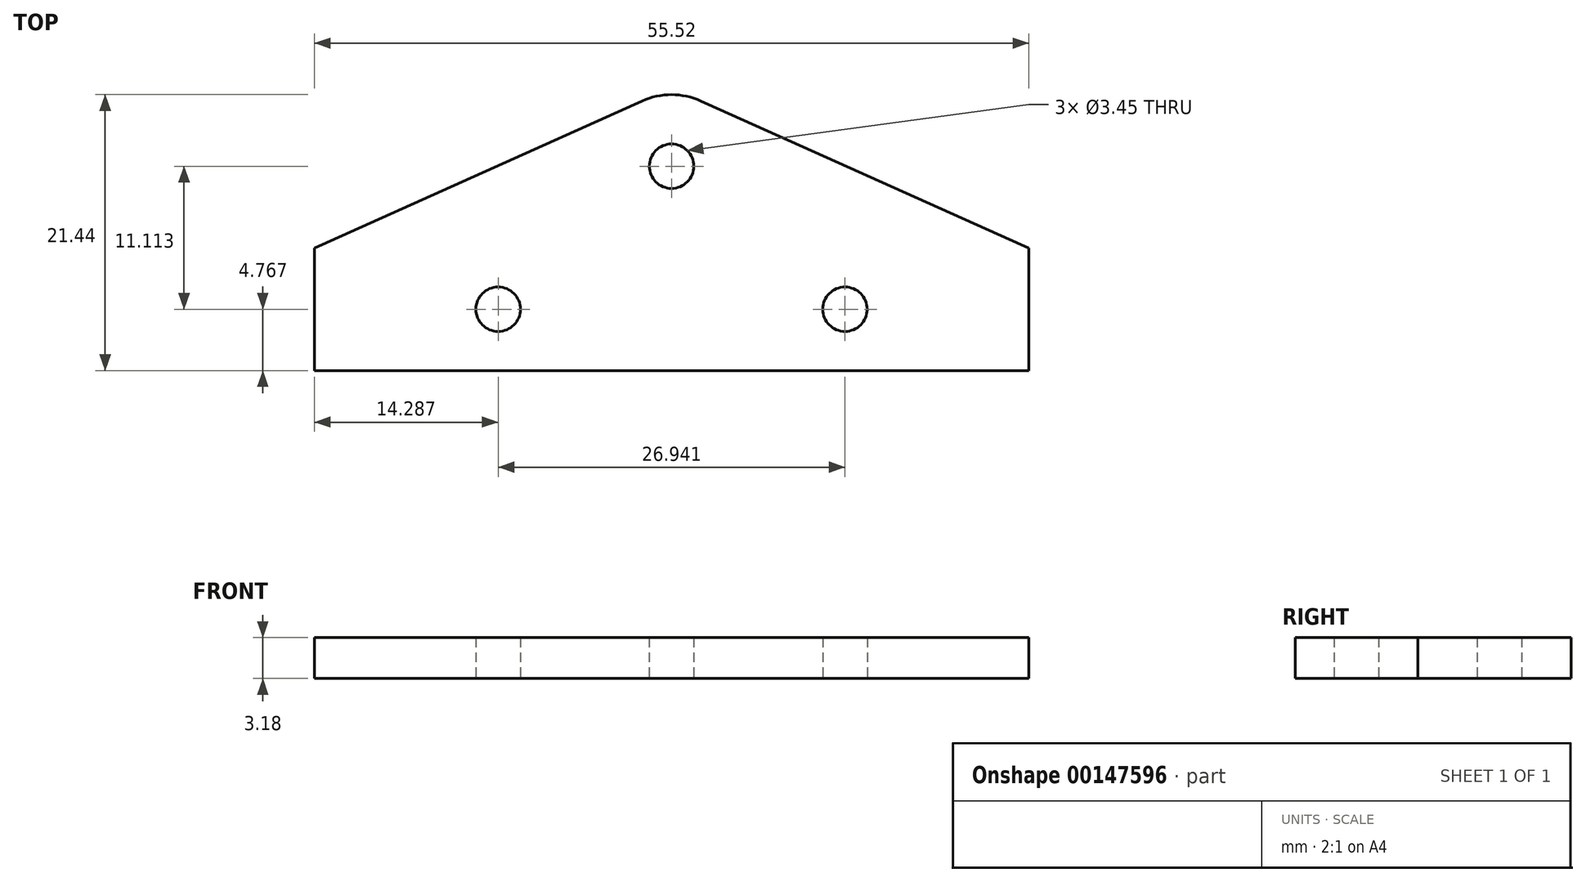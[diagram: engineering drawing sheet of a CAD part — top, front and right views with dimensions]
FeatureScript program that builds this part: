
annotation { "Feature Type Name" : "Feature", "Feature Type Description" : "" }
export const myFeature = defineFeature(function(context is Context, id is Id, definition is map)
    precondition{}
    {
        {
            var Q0;
            Q0=qCreatedBy(makeId("Top.planeOp"),FACE);
            var sketch = newSketch(context, id + "F0", { "sketchPlane" : qUnion([Q0])});
            skLineSegment(sketch, "E0.bottom", {"start": v(0, 0) * mm, "end": v(55.52, 0) * mm, "construction": true});
            skLineSegment(sketch, "E0.top", {"start": v(0, -9.53) * mm, "end": v(55.52, -9.53) * mm});
            skLineSegment(sketch, "E0.left", {"start": v(0, 0) * mm, "end": v(0, -9.53) * mm});
            skLineSegment(sketch, "E0.right", {"start": v(55.52, 0) * mm, "end": v(55.52, -9.52) * mm});
            skLineSegment(sketch, "E1", {"start": v(0, -4.76) * mm, "end": v(14.29, -4.76) * mm, "construction": true});
            skLineSegment(sketch, "E2", {"start": v(55.52, -4.76) * mm, "end": v(41.23, -4.76) * mm, "construction": true});
            skLineSegment(sketch, "E3", {"start": v(27.76, 0) * mm, "end": v(27.76, 6.35) * mm, "construction": true});
            skArc(sketch, "E4", {"start": v(30.03, 11.42) * mm, "mid": v(27.76, 11.9) * mm, "end": v(25.49, 11.42) * mm});
            skLineSegment(sketch, "E5", {"start": v(0, 0) * mm, "end": v(25.49, 11.42) * mm});
            skLineSegment(sketch, "E6", {"start": v(30.03, 11.42) * mm, "end": v(55.52, 0) * mm});
            skCircle(sketch, "E7", {"center": v(14.29, -4.76) * mm, "radius": 1.73 * mm});
            skCircle(sketch, "E8", {"center": v(41.23, -4.76) * mm, "radius": 1.73 * mm});
            skCircle(sketch, "E9", {"center": v(27.76, 6.35) * mm, "radius": 1.73 * mm});
            skSolve(sketch);
        }
        {
            var Q0;
            Q0=qSketchRegion(id+"F0",true);
            extrude(context, id + "F1", {"entities" : qUnion([Q0]), "depth" : 3.17 * mm});
        }
    });
